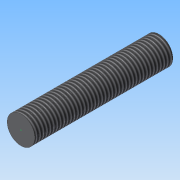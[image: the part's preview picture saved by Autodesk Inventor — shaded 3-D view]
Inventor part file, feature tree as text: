
AUTODESK INVENTOR PART (.ipt)
format: ipt  version: 2015 (Build 190159000, 159)  size: 85,504 bytes
history: native  units: mm
features: sketch x3, extrude x1, thread x1
ambient origin geometry x8: Origin, YZ Plane, XZ Plane, XY Plane, X Axis, Y Axis, Z Axis, Center Point
bodies: Solid1 (feature_tree)
feature tree (5):
  sketch  "Sketch1"  dims[d0=10.0mm d1=50.0mm d2=0.0mm d3=10.0mm d4=0.0mm]
  sketch  "Sketch2"
  extrude  "Extrusion1"  Depth=50.0mm TaperAngle=0.0deg
  thread  "Thread1"  [1 undecoded]
  sketch  "Sketch3"
note: 1 required parameter value undecoded (feature->parameter linkage not recoverable at this tier; creation-order binding heuristic only, values carry confidence <= 0.55)
